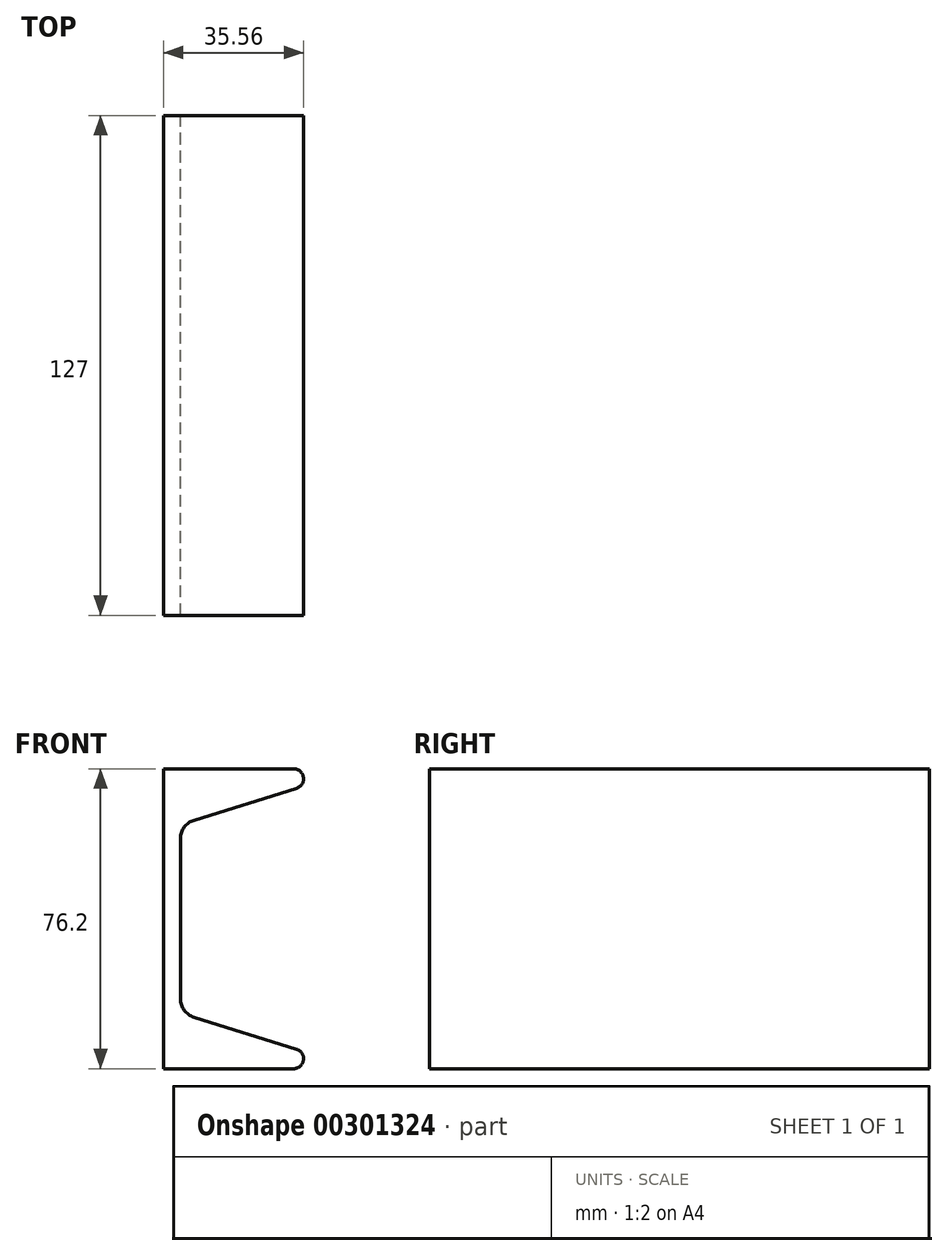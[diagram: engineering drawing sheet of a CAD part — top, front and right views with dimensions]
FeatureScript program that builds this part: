
annotation { "Feature Type Name" : "Feature", "Feature Type Description" : "" }
export const myFeature = defineFeature(function(context is Context, id is Id, definition is map)
    precondition{}
    {
        {
            var Q0;
            Q0=qCreatedBy(makeId("Front.planeOp"),FACE);
            var sketch = newSketch(context, id + "F0", { "sketchPlane" : qUnion([Q0])});
            skLineSegment(sketch, "E0", {"start": v(-68.54, 0) * mm, "end": v(-68.54, 38.1) * mm});
            skLineSegment(sketch, "E1", {"start": v(-68.54, 38.1) * mm, "end": v(-35.52, 38.1) * mm});
            skLineSegment(sketch, "E2", {"start": v(-34.77, 33.13) * mm, "end": v(-60.82, 25.02) * mm});
            skLineSegment(sketch, "E3", {"start": v(-64.23, 20.4) * mm, "end": v(-64.23, 0) * mm});
            skPoint(sketch, "E4.visualSharp", {"position": v(-18.82, 38.1) * mm});
            skArc(sketch, "E4.filletArc", {"start": v(-34.77, 33.13) * mm, "mid": v(-33.01, 35.94) * mm, "end": v(-35.52, 38.1) * mm});
            skPoint(sketch, "E5.visualSharp", {"position": v(-64.23, 23.96) * mm});
            skArc(sketch, "E5.filletArc", {"start": v(-60.82, 25.02) * mm, "mid": v(-63.28, 23.27) * mm, "end": v(-64.23, 20.4) * mm});
            skArc(sketch, "E6.MirrorCS", {"start": v(-34.77, -33.13) * mm, "mid": v(-33.01, -35.94) * mm, "end": v(-35.52, -38.1) * mm});
            skArc(sketch, "E7.MirrorCS", {"start": v(-60.82, -25.02) * mm, "mid": v(-63.28, -23.27) * mm, "end": v(-64.23, -20.4) * mm});
            skLineSegment(sketch, "E8.MirrorCS", {"start": v(-68.54, -38.1) * mm, "end": v(-35.52, -38.1) * mm});
            skPoint(sketch, "E9.MirrorP", {"position": v(-18.82, -38.1) * mm});
            skLineSegment(sketch, "E10.MirrorCS", {"start": v(-64.23, -20.4) * mm, "end": v(-64.23, 0) * mm});
            skLineSegment(sketch, "E11.MirrorCS", {"start": v(-34.77, -33.13) * mm, "end": v(-60.82, -25.02) * mm});
            skPoint(sketch, "E12.MirrorP", {"position": v(-64.23, -23.96) * mm});
            skLineSegment(sketch, "E13.MirrorCS", {"start": v(-68.54, 0) * mm, "end": v(-68.54, -38.1) * mm});
            skSolve(sketch);
        }
        {
            var Q0;
            Q0 = qSketchRegion(id + "F0", true);
            extrude(context, id + "F1", {"entities" : qUnion([Q0]), "endBound" : BoundingType.SYMMETRIC, "depth" : 127 * mm});
        }
    });
